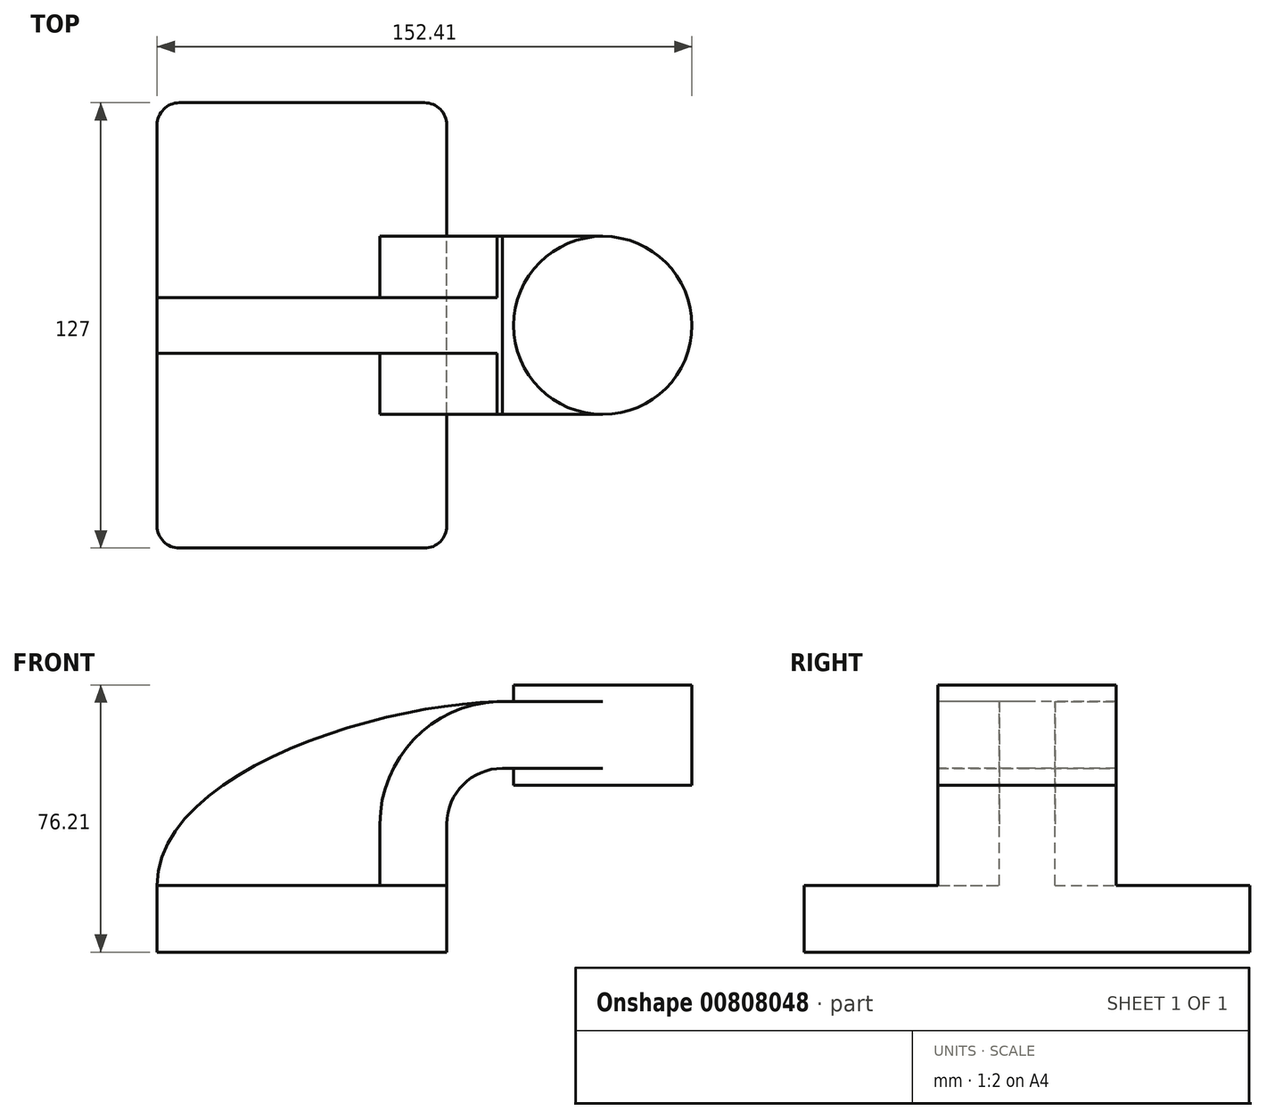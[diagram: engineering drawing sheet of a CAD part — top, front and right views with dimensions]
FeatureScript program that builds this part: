
annotation { "Feature Type Name" : "Feature", "Feature Type Description" : "" }
export const myFeature = defineFeature(function(context is Context, id is Id, definition is map)
    precondition{}
    {
        {
            var Q0;
            Q0=qCreatedBy(makeId("Front.planeOp"),FACE);
            var sketch = newSketch(context, id + "F0", { "sketchPlane" : qUnion([Q0])});
            skLineSegment(sketch, "E0.bottom", {"start": v(41.27, 9.53) * mm, "end": v(-41.27, 9.53) * mm});
            skLineSegment(sketch, "E0.top", {"start": v(41.28, -9.52) * mm, "end": v(-41.27, -9.52) * mm});
            skLineSegment(sketch, "E0.left", {"start": v(41.27, 9.53) * mm, "end": v(41.28, -9.52) * mm});
            skLineSegment(sketch, "E0.right", {"start": v(-41.27, 9.53) * mm, "end": v(-41.27, -9.52) * mm});
            skPoint(sketch, "E0.middle", {"position": v(0, 0) * mm});
            skLineSegment(sketch, "E1.bottom", {"start": v(111.12, 66.68) * mm, "end": v(60.33, 66.68) * mm});
            skLineSegment(sketch, "E1.top", {"start": v(111.12, 38.1) * mm, "end": v(60.33, 38.1) * mm});
            skLineSegment(sketch, "E1.left", {"start": v(111.12, 66.68) * mm, "end": v(111.12, 38.1) * mm});
            skLineSegment(sketch, "E1.right", {"start": v(60.33, 66.67) * mm, "end": v(60.33, 38.1) * mm});
            skPoint(sketch, "E1.middle", {"position": v(85.72, 52.39) * mm});
            skLineSegment(sketch, "E2", {"start": v(41.27, 9.53) * mm, "end": v(41.27, 27) * mm});
            skArc(sketch, "E3", {"start": v(41.27, 27) * mm, "mid": v(45.92, 38.23) * mm, "end": v(57.15, 42.88) * mm});
            skLineSegment(sketch, "E4", {"start": v(57.15, 42.88) * mm, "end": v(85.72, 42.88) * mm});
            skArc(sketch, "E5.0", {"start": v(22.22, 27) * mm, "mid": v(32.45, 51.7) * mm, "end": v(57.15, 61.93) * mm});
            skLineSegment(sketch, "E5.1", {"start": v(22.22, 9.53) * mm, "end": v(22.22, 27) * mm});
            skLineSegment(sketch, "E6.0", {"start": v(57.15, 61.93) * mm, "end": v(85.72, 61.93) * mm});
            skLineSegment(sketch, "E7", {"start": v(85.72, 38.1) * mm, "end": v(85.72, 66.68) * mm});
            skFitSpline(sketch, "E8", {"points": [v(-41.28, 9.53) * mm, v(57.15, 61.93) * mm], "startDerivative": vector(0.7, 97.28) * mm, "endDerivative": vector(105.68, 1.57) * mm});
            skSolve(sketch);
        }
        {
            var Q0;
            Q0=makeQuery(id+"F0.imprint","IMPRINT",FACE,{"disambiguationData":[TD([[makeQuery(id+"F0.imprint","IMPRINT",EDGE,{"derivedFrom":sQuery(id+"F0.wireOp",EDGE,"E0.top")}),-1.0]])]});
            extrude(context, id + "F1", {"entities" : qUnion([Q0]), "endBound" : BoundingType.SYMMETRIC, "depth" : 127 * mm, "offsetDistance" : 25.4 * mm});
        }
        {
            var Q0;
            {var subQ0=sQuery(id+"F0.wireOp",EDGE,"E6.0");var subQ1=sQuery(id+"F0.wireOp",EDGE,"E1.right");var subQ2=makeQuery(id+"F0.imprint","INTERSECT",VERTEX,{"derivedFrom":[subQ1,subQ0]});Q0=makeQuery(id+"F0.imprint","IMPRINT",FACE,{"disambiguationData":[TD([[makeQuery(id+"F0.imprint","IMPRINT",EDGE,{"disambiguationData":[TD([[subQ2,-1.0]])],"derivedFrom":subQ1}),1.0]])]});}
            var Q1;
            {var subQ1=sQuery(id+"F0.wireOp",EDGE,"E2");Q1=makeQuery(id+"F0.imprint","IMPRINT",FACE,{"disambiguationData":[TD([[makeQuery(id+"F0.imprint","IMPRINT",EDGE,{"derivedFrom":subQ1}),1.0]])]});}
            extrude(context, id + "F2", {"entities" : qUnion([Q0, Q1]), "operationType" : NewBodyOperationType.ADD, "endBound" : BoundingType.SYMMETRIC, "depth" : 50.8 * mm, "offsetDistance" : 25.4 * mm});
        }
        {
            var Q0;
            {var subQ3=sQuery(id+"F0.wireOp",EDGE,"E5.1");Q0=makeQuery(id+"F0.imprint","IMPRINT",FACE,{"disambiguationData":[TD([[makeQuery(id+"F0.imprint","IMPRINT",EDGE,{"derivedFrom":subQ3}),1.0]])]});}
            extrude(context, id + "F3", {"entities" : qUnion([Q0]), "operationType" : NewBodyOperationType.ADD, "endBound" : BoundingType.SYMMETRIC, "depth" : 15.88 * mm, "offsetDistance" : 25.4 * mm});
        }
        {
            var Q0;
            {var subQ0=sQuery(id+"F0.wireOp",EDGE,"E1.left");Q0=makeQuery(id+"F0.imprint","IMPRINT",FACE,{"disambiguationData":[TD([[makeQuery(id+"F0.imprint","IMPRINT",EDGE,{"derivedFrom":subQ0}),-1.0]])]});}
            var Q1;
            Q1=sQuery(id+"F0.wireOp",EDGE,"E7");
            revolve(context, id + "F4", {"operationType" : NewBodyOperationType.ADD, "surfaceOperationType" : NewSurfaceOperationType.NEW, "entities" : qUnion([Q0]), "axis" : qUnion([Q1]), "revolveType" : RevolveType.FULL});
        }
        {
            var Q0;
            Q0=makeQuery(id+"F1.opExtrude","CAP_EDGE",EDGE,{"disambiguationData":[OSD([sQuery(id+"F0.wireOp",EDGE,"E0.left")])],"isStart":false});
            var Q1;
            Q1=makeQuery(id+"F1.opExtrude","CAP_EDGE",EDGE,{"disambiguationData":[OSD([sQuery(id+"F0.wireOp",EDGE,"E0.left")])],"isStart":true});
            var Q2;
            Q2=makeQuery(id+"F1.opExtrude","CAP_EDGE",EDGE,{"disambiguationData":[OSD([sQuery(id+"F0.wireOp",EDGE,"E0.right")])],"isStart":false});
            var Q3;
            Q3=makeQuery(id+"F1.opExtrude","CAP_EDGE",EDGE,{"disambiguationData":[OSD([sQuery(id+"F0.wireOp",EDGE,"E0.right")])],"isStart":true});
            fillet(context, id + "F5", {"entities" : qUnion([Q0, Q1, Q2, Q3]), "radius" : 6.35 * mm, "tangentPropagation" : true, "allowEdgeOverflow" : false});
        }
    });
